# Revit family: 2L-P-ID
name_source: partatom
category: Lighting Fixtures
revit_build: Autodesk Revit 2014 (Build: 20130308_1515(x64)
units: mm (PartAtom-declared; Revit-internal decimal feet)

## types (6) — shared parameters
Apparent Load = 12 VA
Assembly Code = D5020200
Color Filter = 16777215
Connector Description = Lighting Connector
Default Elevation = 48"
Description = MOD 2 LED Pendant Indirect/Direct
Dimming Lamp Color Temperature Shift = <None>
Emit Shape Visible in Rendering = No
Emit from Rectangle Length = 24"
Emit from Rectangle Width = 2"
Fixture distribution = Indirect/Direct
Housing Material = Paint - Hubbell - Matte White
Lamp = LED
Load Classification = Lighting
Manufacturer = LITECONTROL
Model = 2L-P-ID
Photometric Web File = 2L-P-AD-4-ASYM-X-CX-35K-D030.ies
Power Factor = 1
Product Documentation Link = https://hubbellcdn.com
Product Link = https://www.hubbell.com
Reflector Finish = Hubbell - White Glass
Tilt Angle = -90.00°
URL = https://www.hubbell.com
Uplight distribution = Standard
Voltage = 120 V
Warranty = 5 years Warranty
Wattage Comments = Variable Intensity technology provides specifiable lumen output/wattage
Watts = 12 W

## per-type parameters (varying)
| type | Max Length in Row |
| 2L-P-ID-02 | 2L-P : 02 |
| 2L-P-ID-03 | 2L-P : 03 |
| 2L-P-ID-04 | 2L-P : 04 |
| 2L-P-ID-05 | 2L-P : 05 |
| 2L-P-ID-06 | 2L-P : 06 |
| 2L-P-ID-08 | 2L-P : 08 |

## geometry (parser evidence)
native form markers: Blend x13, Sweep x3
no freeform markers — native parametric forms only
